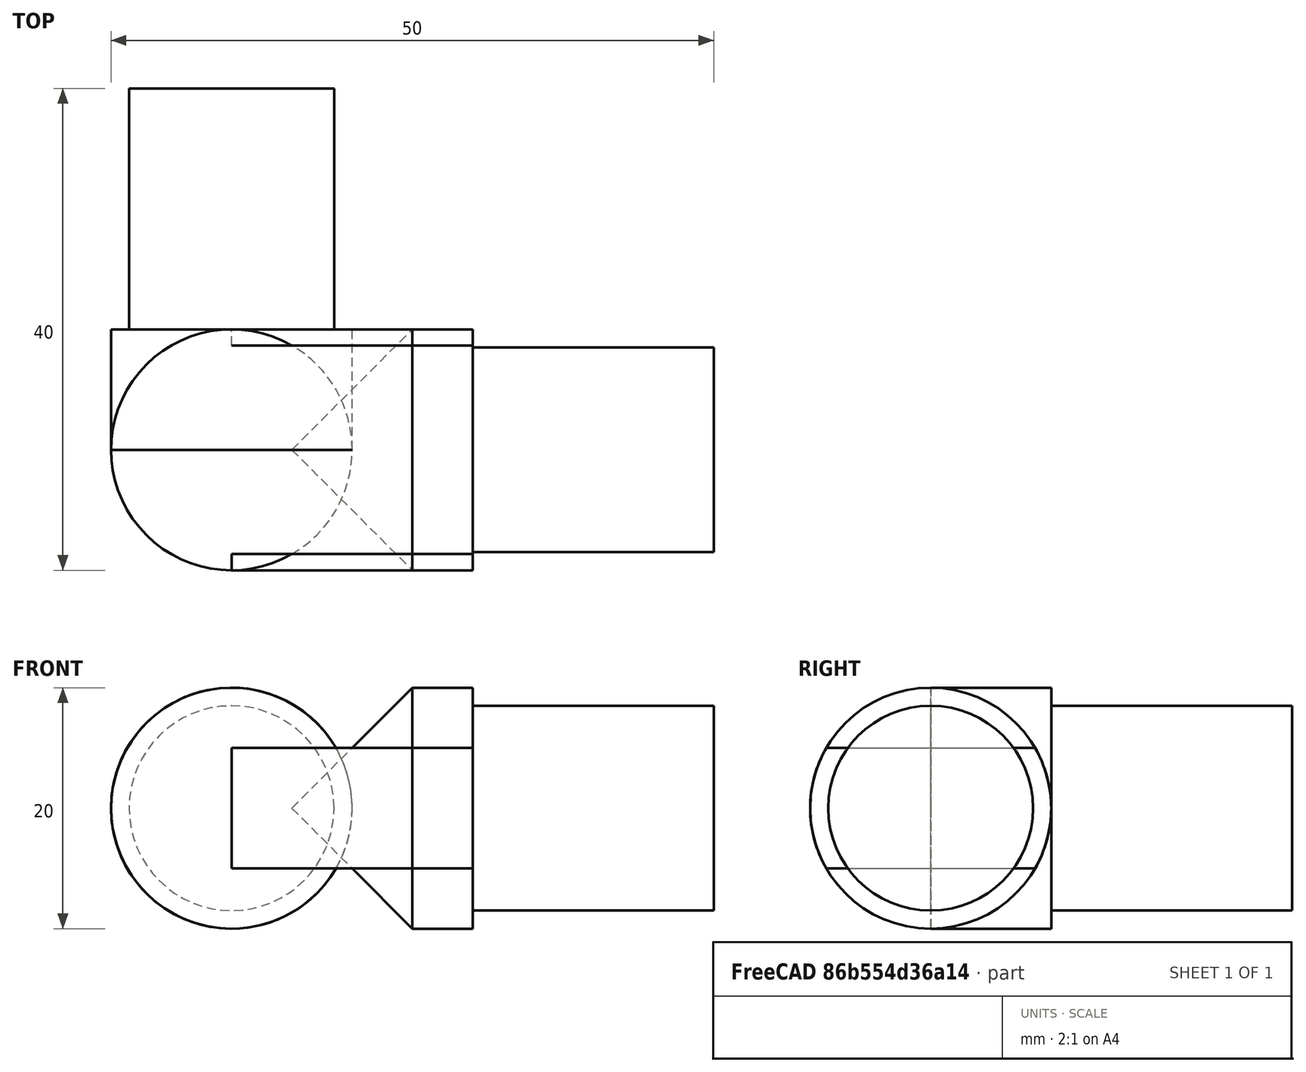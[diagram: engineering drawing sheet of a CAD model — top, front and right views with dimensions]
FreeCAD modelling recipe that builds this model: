
FCSTD DOCUMENT  (FreeCAD 0.18R16110 (Git))
Label: connector-rail
License: All rights reserved
LicenseURL: http://en.wikipedia.org/wiki/All_rights_reserved
objects: Part::Cylinder×5, Part::Sphere×1, Part::MultiFuse×1, Part::FeaturePython×1, Part::Box×1, Part::Cone×1, Part::MultiCommon×1
note: 11 computed .brp shape members not serialized (recipe doc carries the construction recipe); baked Part::Feature solids carry a one-line shape summary decoded from their .brp

FEATURE [Part::Sphere] Sphere
  Angle1 = -90
  Angle2 = 90
  Angle3 = 360
  AttacherType = Attacher::AttachEngine3D
  Radius = 10
FEATURE [Part::Cylinder] Cylinder003
  Angle = 360
  AttacherType = Attacher::AttachEngine3D
  Height = 10
  Placement = pos=(0,0,2e-15) rot=(0,0.707107,-0.707107;3.14159rad)
  Radius = 10
FEATURE [Part::Cylinder] Cylinder004
  Angle = 360
  AttacherType = Attacher::AttachEngine3D
  Height = 30
  Placement = pos=(0,0,2e-15) rot=(0,0.707107,-0.707107;3.14159rad)
  Radius = 8.5
FEATURE [Part::MultiFuse] Fusion  label="Pipe Join"
  Shapes = -> [Cylinder003,Cylinder004]
FEATURE [Part::FeaturePython] Clone  label="Pipe Join001"  # Draft clone (typed FeaturePython)
  AttacherType = Attacher::AttachEngine3D
  Fuse = false
  Objects = -> [Fusion]
  Placement = pos=(0,0,0) rot=(0,0,1;3.14159rad)
  Scale = (1,1,1)
FEATURE [Part::Cylinder] Cylinder005
  Angle = 360
  AttacherType = Attacher::AttachEngine3D
  Height = 20
  Placement = pos=(20,4e-15,2e-15) rot=(0.57735,-0.57735,0.57735;4.18879rad)
  Radius = 8.5
FEATURE [Part::Box] Box  label="Cube"
  AttacherType = Attacher::AttachEngine3D
  Height = 10
  Length = 20
  Placement = pos=(0,-10,-5) rot=(0,0,1;0rad)
  Width = 20
FEATURE [Part::Cone] Cone
  Angle = 360
  AttacherType = Attacher::AttachEngine3D
  Height = 10
  Placement = pos=(5,0,1.1e-15) rot=(0,1,0;1.5708rad)
  Radius1 = 0
  Radius2 = 10
FEATURE [Part::Cylinder] Cylinder
  Angle = 360
  AttacherType = Attacher::AttachEngine3D
  Height = 20
  Placement = pos=(0,0,0) rot=(0,1,0;1.5708rad)
  Radius = 10
FEATURE [Part::MultiCommon] Common
  Shapes = -> [Box,Cylinder]
FEATURE [Part::Cylinder] Cylinder006
  Angle = 360
  AttacherType = Attacher::AttachEngine3D
  Height = 5
  Placement = pos=(15,0,3e-15) rot=(0,1,0;1.5708rad)
  Radius = 10
